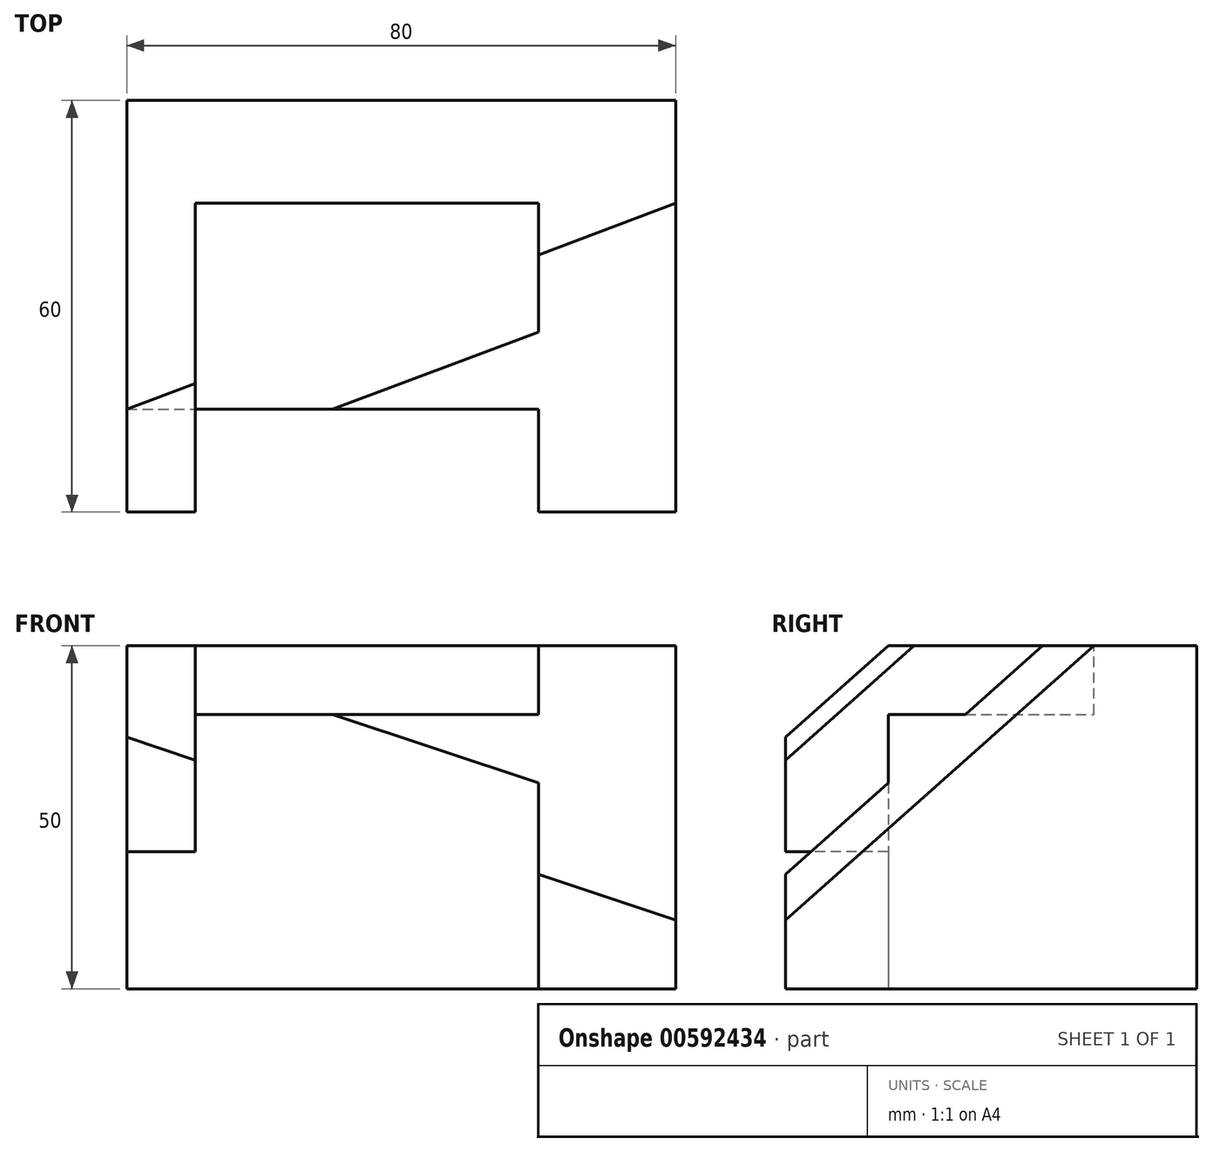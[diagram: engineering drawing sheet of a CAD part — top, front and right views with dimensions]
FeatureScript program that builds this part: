
annotation { "Feature Type Name" : "Feature", "Feature Type Description" : "" }
export const myFeature = defineFeature(function(context is Context, id is Id, definition is map)
    precondition{}
    {
        {
            var Q0;
            Q0=qCreatedBy(makeId("Front.planeOp"),FACE);
            var sketch = newSketch(context, id + "F0", { "sketchPlane" : qUnion([Q0])});
            skLineSegment(sketch, "E0.bottom", {"start": v(-40, 25) * mm, "end": v(40, 25) * mm});
            skLineSegment(sketch, "E0.top", {"start": v(-40, -25) * mm, "end": v(40, -25) * mm});
            skLineSegment(sketch, "E0.left", {"start": v(-40, 25) * mm, "end": v(-40, -25) * mm});
            skLineSegment(sketch, "E0.right", {"start": v(40, 25) * mm, "end": v(40, -25) * mm});
            skSolve(sketch);
        }
        {
            var Q0;
            Q0 = qSketchRegion(id + "F0", true);
            extrude(context, id + "F1", {"entities" : qUnion([Q0]), "depth" : 60 * mm, "offsetDistance" : 25 * mm, "symmetric" : true});
        }
        {
            var Q0;
            Q0=makeQuery(id+"F1.opExtrude","SWEPT_FACE",FACE,{"disambiguationData":[OSD([sQuery(id+"F0.wireOp",EDGE,"E0.bottom")])]});
            var sketch = newSketch(context, id + "F2", { "sketchPlane" : qUnion([Q0])});
            skLineSegment(sketch, "E1.bottom", {"start": v(-30, -30) * mm, "end": v(20, -30) * mm});
            skLineSegment(sketch, "E1.top", {"start": v(-30, 15) * mm, "end": v(20, 15) * mm});
            skLineSegment(sketch, "E1.left", {"start": v(-30, -30) * mm, "end": v(-30, 15) * mm});
            skLineSegment(sketch, "E1.right", {"start": v(20, -30) * mm, "end": v(20, 15) * mm});
            skSolve(sketch);
        }
        {
            var Q0;
            Q0 = qSketchRegion(id + "F2", true);
            extrude(context, id + "F3", {"entities" : qUnion([Q0]), "operationType" : NewBodyOperationType.REMOVE, "oppositeDirection" : true, "depth" : 10 * mm, "offsetDistance" : 25 * mm});
        }
        {
            var Q0;
            Q0=makeQuery(id+"F1.opExtrude","CAP_FACE",FACE,{"disambiguationData":[OSD([sQuery(id+"F0.wireOp",EDGE,"E0.bottom"),sQuery(id+"F0.wireOp",EDGE,"E0.top"),sQuery(id+"F0.wireOp",EDGE,"E0.left"),sQuery(id+"F0.wireOp",EDGE,"E0.right")])],"isStart":false});
            var sketch = newSketch(context, id + "F4", { "sketchPlane" : qUnion([Q0])});
            skLineSegment(sketch, "E2.bottom", {"start": v(-30, 15) * mm, "end": v(20, 15) * mm});
            skLineSegment(sketch, "E2.top", {"start": v(-30, -25) * mm, "end": v(20, -25) * mm});
            skLineSegment(sketch, "E2.left", {"start": v(-30, 15) * mm, "end": v(-30, -25) * mm});
            skLineSegment(sketch, "E2.right", {"start": v(20, 15) * mm, "end": v(20, -25) * mm});
            skSolve(sketch);
        }
        {
            var Q0;
            Q0 = qSketchRegion(id + "F4", true);
            extrude(context, id + "F5", {"entities" : qUnion([Q0]), "operationType" : NewBodyOperationType.REMOVE, "oppositeDirection" : true, "depth" : 15 * mm, "offsetDistance" : 25 * mm});
        }
        {
            var Q0;
            {var subQ0=sQuery(id+"F0.wireOp",EDGE,"E0.left");var subQ1=sQuery(id+"F0.wireOp",EDGE,"E0.top");var subQ2=sQuery(id+"F0.wireOp",EDGE,"E0.bottom");Q0=makeQuery(id+"F5.boolean.opBoolean","SPLIT",FACE,{"disambiguationData":[TD([makeQuery(id+"F1.opExtrude","SWEPT_FACE",FACE,{"disambiguationData":[OSD([subQ0])]})])],"derivedFrom":makeQuery(id+"F1.opExtrude","CAP_FACE",FACE,{"disambiguationData":[OSD([subQ2,subQ1,subQ0,sQuery(id+"F0.wireOp",EDGE,"E0.right")])],"isStart":false})});}
            var sketch = newSketch(context, id + "F6", { "sketchPlane" : qUnion([Q0])});
            skLineSegment(sketch, "E3.bottom", {"start": v(-40, -25) * mm, "end": v(-30, -25) * mm});
            skLineSegment(sketch, "E3.top", {"start": v(-40, -5) * mm, "end": v(-30, -5) * mm});
            skLineSegment(sketch, "E3.left", {"start": v(-40, -25) * mm, "end": v(-40, -5) * mm});
            skLineSegment(sketch, "E3.right", {"start": v(-30, -25) * mm, "end": v(-30, -5) * mm});
            skSolve(sketch);
        }
        {
            var Q0;
            Q0 = qSketchRegion(id + "F6", true);
            extrude(context, id + "F7", {"entities" : qUnion([Q0]), "operationType" : NewBodyOperationType.REMOVE, "oppositeDirection" : true, "depth" : 15 * mm, "offsetDistance" : 25 * mm});
        }
        {
            var Q0;
            Q0=makeQuery(id+"F1.opExtrude","SWEPT_FACE",FACE,{"disambiguationData":[OSD([sQuery(id+"F0.wireOp",EDGE,"E0.bottom")])]});
            var sketch = newSketch(context, id + "F8", { "sketchPlane" : qUnion([Q0])});
            skPoint(sketch, "E4", {"position": v(40, 15) * mm});
            skPoint(sketch, "E5", {"position": v(-40, -15) * mm});
            skSolve(sketch);
        }
        {
            var Q0;
            Q0=makeQuery(id+"F1.opExtrude","SWEPT_FACE",FACE,{"disambiguationData":[OSD([sQuery(id+"F0.wireOp",EDGE,"E0.right")])]});
            var sketch = newSketch(context, id + "F9", { "sketchPlane" : qUnion([Q0])});
            skPoint(sketch, "E6", {"position": v(-30, -15) * mm});
            skSolve(sketch);
        }
        {
            var Q0;
            Q0=sQuery(id+"F8.wireOp",VERTEX,"E5");
            var Q1;
            Q1=sQuery(id+"F8.wireOp",VERTEX,"E4");
            var Q2;
            Q2=sQuery(id+"F9.wireOp",VERTEX,"E6");
            cPlane(context, id + "F10", {"entities" : qUnion([Q0, Q1, Q2]), "cplaneType" : CPlaneType.THREE_POINT, "offset" : 25 * mm, "width" : 150 * mm, "height" : 150 * mm});
        }
        {
            var Q0;
            Q0=qCreatedBy(id+"F10.planeOp",FACE);
            var sketch = newSketch(context, id + "F11", { "sketchPlane" : qUnion([Q0])});
            skLineSegment(sketch, "E7.bottom", {"start": v(-54.23, -36.64) * mm, "end": v(44.2, -36.64) * mm});
            skLineSegment(sketch, "E7.top", {"start": v(-54.23, 33.28) * mm, "end": v(44.2, 33.28) * mm});
            skLineSegment(sketch, "E7.left", {"start": v(-54.23, -36.64) * mm, "end": v(-54.23, 33.28) * mm});
            skLineSegment(sketch, "E7.right", {"start": v(44.2, -36.64) * mm, "end": v(44.2, 33.28) * mm});
            skSolve(sketch);
        }
        {
            var Q0;
            Q0 = qSketchRegion(id + "F11", true);
            extrude(context, id + "F12", {"entities" : qUnion([Q0]), "operationType" : NewBodyOperationType.REMOVE, "depth" : 30 * mm, "offsetDistance" : 25 * mm});
        }
    });
